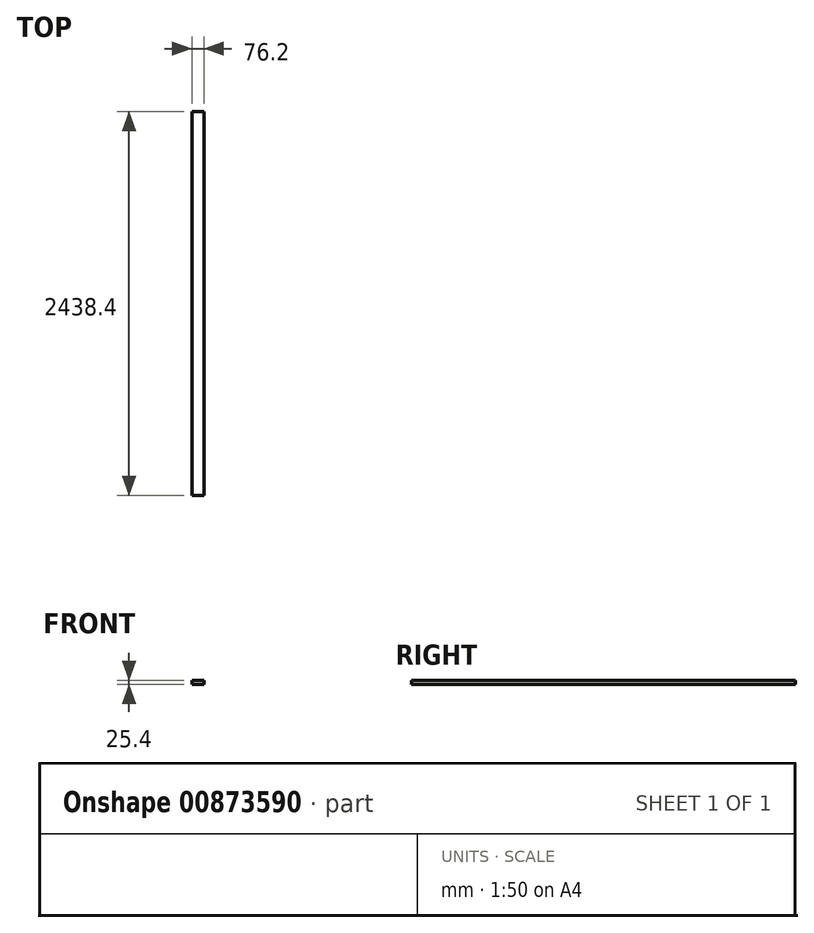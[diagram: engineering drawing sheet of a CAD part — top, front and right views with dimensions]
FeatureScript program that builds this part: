
annotation { "Feature Type Name" : "Feature", "Feature Type Description" : "" }
export const myFeature = defineFeature(function(context is Context, id is Id, definition is map)
    precondition{}
    {
        {
            var Q0;
            Q0=qCreatedBy(makeId("Top.planeOp"),FACE);
            var sketch = newSketch(context, id + "F0", { "sketchPlane" : qUnion([Q0])});
            skLineSegment(sketch, "E0.bottom", {"start": v(0, 0) * mm, "end": v(76.2, 0) * mm});
            skLineSegment(sketch, "E0.top", {"start": v(0, 2438.4) * mm, "end": v(76.2, 2438.4) * mm});
            skLineSegment(sketch, "E0.left", {"start": v(0, 0) * mm, "end": v(0, 2438.4) * mm});
            skLineSegment(sketch, "E0.right", {"start": v(76.2, 0) * mm, "end": v(76.2, 2438.4) * mm});
            skSolve(sketch);
        }
        {
            var Q0;
            Q0=qSketchRegion(id+"F0",true);
            extrude(context, id + "F1", {"entities" : qUnion([Q0]), "depth" : 25.4 * mm, "offsetDistance" : 25.4 * mm});
        }
    });
